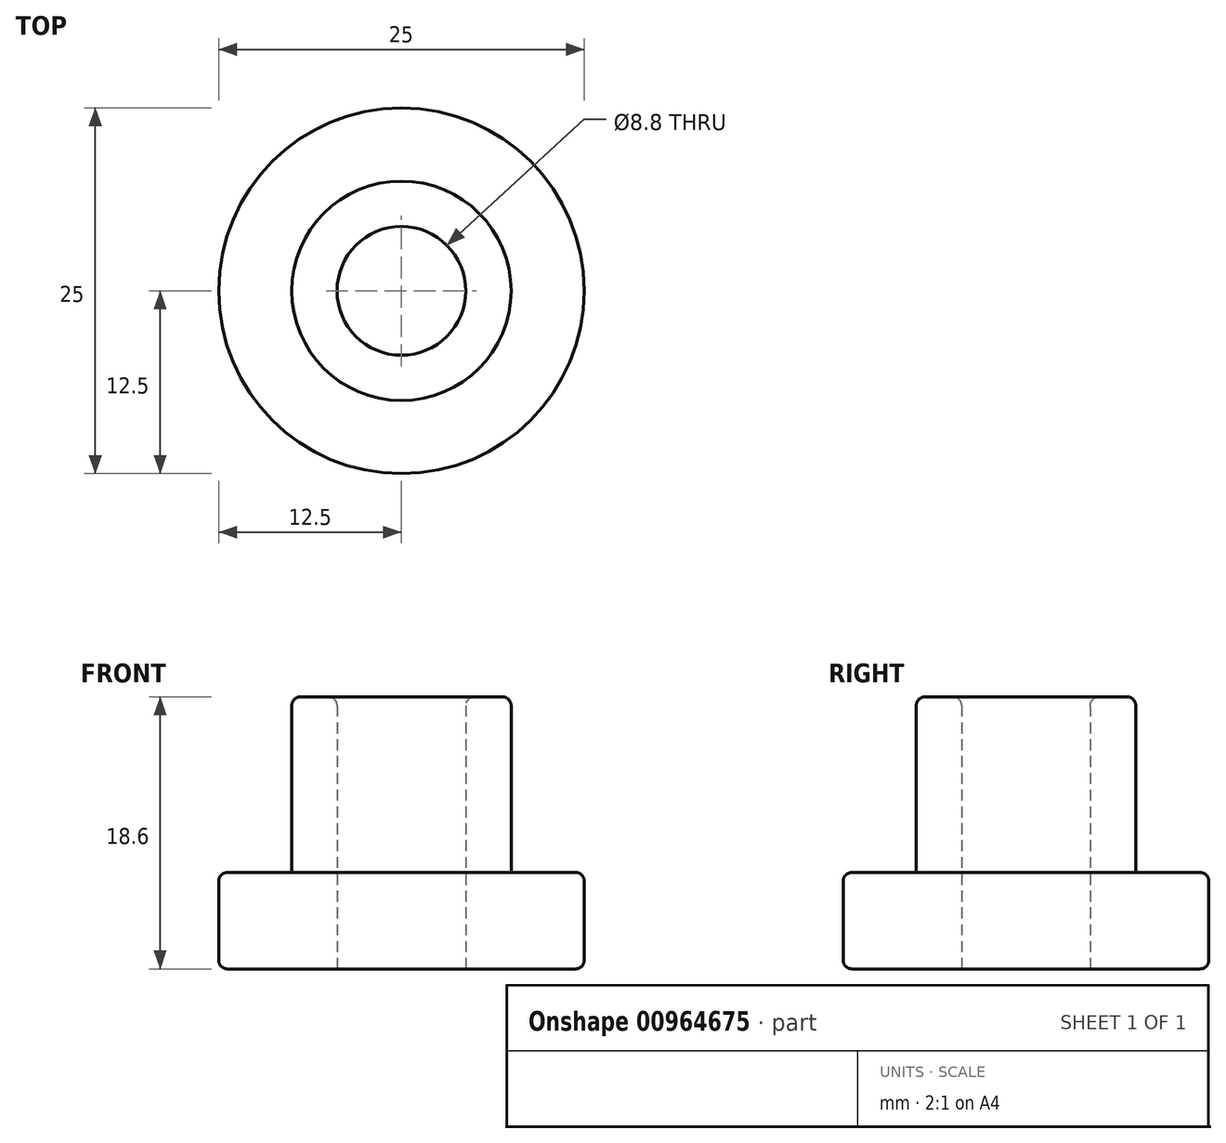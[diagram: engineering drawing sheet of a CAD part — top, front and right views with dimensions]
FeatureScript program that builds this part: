
annotation { "Feature Type Name" : "Feature", "Feature Type Description" : "" }
export const myFeature = defineFeature(function(context is Context, id is Id, definition is map)
    precondition{}
    {
        {
            var Q0;
            Q0=qCreatedBy(makeId("Top.planeOp"),FACE);
            var sketch = newSketch(context, id + "F0", { "sketchPlane" : qUnion([Q0])});
            skCircle(sketch, "E0", {"center": v(0, 0) * mm, "radius": 12.5 * mm});
            skSolve(sketch);
        }
        {
            var Q0;
            Q0 = qSketchRegion(id + "F0", true);
            extrude(context, id + "F1", {"entities" : qUnion([Q0]), "depth" : 6.6 * mm, "offsetDistance" : 25 * mm});
        }
        {
            var Q0;
            Q0=makeQuery(id+"F1.opExtrude","CAP_FACE",FACE,{"disambiguationData":[OSD([sQuery(id+"F0.wireOp",EDGE,"E0")])],"isStart":false});
            var sketch = newSketch(context, id + "F2", { "sketchPlane" : qUnion([Q0])});
            skCircle(sketch, "E1", {"center": v(0, 0) * mm, "radius": 7.5 * mm});
            skSolve(sketch);
        }
        {
            var Q0;
            Q0 = qSketchRegion(id + "F2", true);
            extrude(context, id + "F3", {"entities" : qUnion([Q0]), "operationType" : NewBodyOperationType.ADD, "depth" : 12 * mm, "offsetDistance" : 25 * mm});
        }
        {
            var Q0;
            Q0=qCreatedBy(makeId("Top.planeOp"),FACE);
            var sketch = newSketch(context, id + "F4", { "sketchPlane" : qUnion([Q0])});
            skCircle(sketch, "E2", {"center": v(0, 0) * mm, "radius": 4.4 * mm});
            skSolve(sketch);
        }
        {
            var Q0;
            Q0 = qSketchRegion(id + "F4", true);
            extrude(context, id + "F5", {"entities" : qUnion([Q0]), "operationType" : NewBodyOperationType.REMOVE, "endBound" : BoundingType.THROUGH_ALL, "depth" : 25 * mm, "offsetDistance" : 25 * mm});
        }
        {
            var Q0;
            Q0=makeQuery(id+"F5.boolean.opBoolean","INTERSECT",EDGE,{"derivedFrom":[makeQuery(id+"F3.opExtrude","CAP_FACE",FACE,{"disambiguationData":[OSD([sQuery(id+"F2.wireOp",EDGE,"E1")])],"isStart":false}),makeQuery(id+"F5.opExtrude","SWEPT_FACE",FACE,{"disambiguationData":[OSD([sQuery(id+"F4.wireOp",EDGE,"E2")])]})]});
            var Q1;
            Q1=makeQuery(id+"F3.opExtrude","CAP_EDGE",EDGE,{"disambiguationData":[OSD([sQuery(id+"F2.wireOp",EDGE,"E1")])],"isStart":false});
            var Q2;
            Q2=makeQuery(id+"F3.opExtrude","CAP_EDGE",EDGE,{"disambiguationData":[OSD([sQuery(id+"F2.wireOp",EDGE,"E1")])],"isStart":true});
            var Q3;
            Q3=makeQuery(id+"F1.opExtrude","SWEPT_FACE",FACE,{"disambiguationData":[OSD([sQuery(id+"F0.wireOp",EDGE,"E0")])]});
            var Q4;
            Q4=makeQuery(id+"F5.boolean.opBoolean","COPY",EDGE,{"derivedFrom":makeQuery(id+"F5.opExtrude","CAP_EDGE",EDGE,{"disambiguationData":[OSD([sQuery(id+"F4.wireOp",EDGE,"E2")])],"isStart":true})});
            fillet(context, id + "F6", {"entities" : qUnion([Q0, Q1, Q2, Q3, Q4]), "radius" : .6 * mm, "tangentPropagation" : true, "allowEdgeOverflow" : false});
        }
    });
